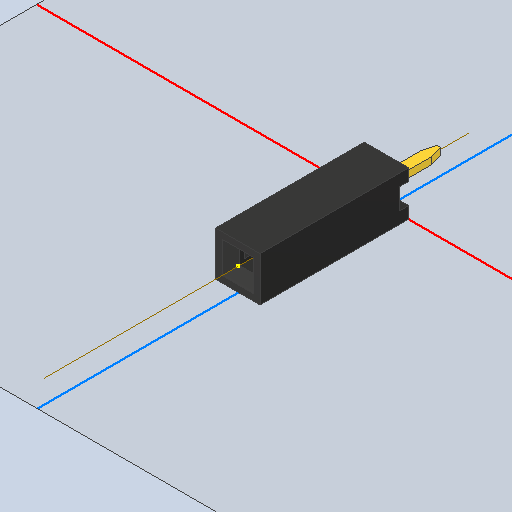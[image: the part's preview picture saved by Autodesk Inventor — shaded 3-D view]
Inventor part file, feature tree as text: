
AUTODESK INVENTOR PART (.ipt)
format: ipt  version: 2022 (Build 260153000, 153)  size: 142,848 bytes
history: native  units: mm
features: sketch x1, other x1, imported_body x1
ambient origin geometry x8: Origin, YZ Plane, XZ Plane, XY Plane, X Axis, Y Axis, Z Axis, Center Point
bodies: Solid1 (feature_tree)
feature tree (3):
  sketch  "Sketch1"
  other  "Work Axis1"
  imported_body  "Base1"
